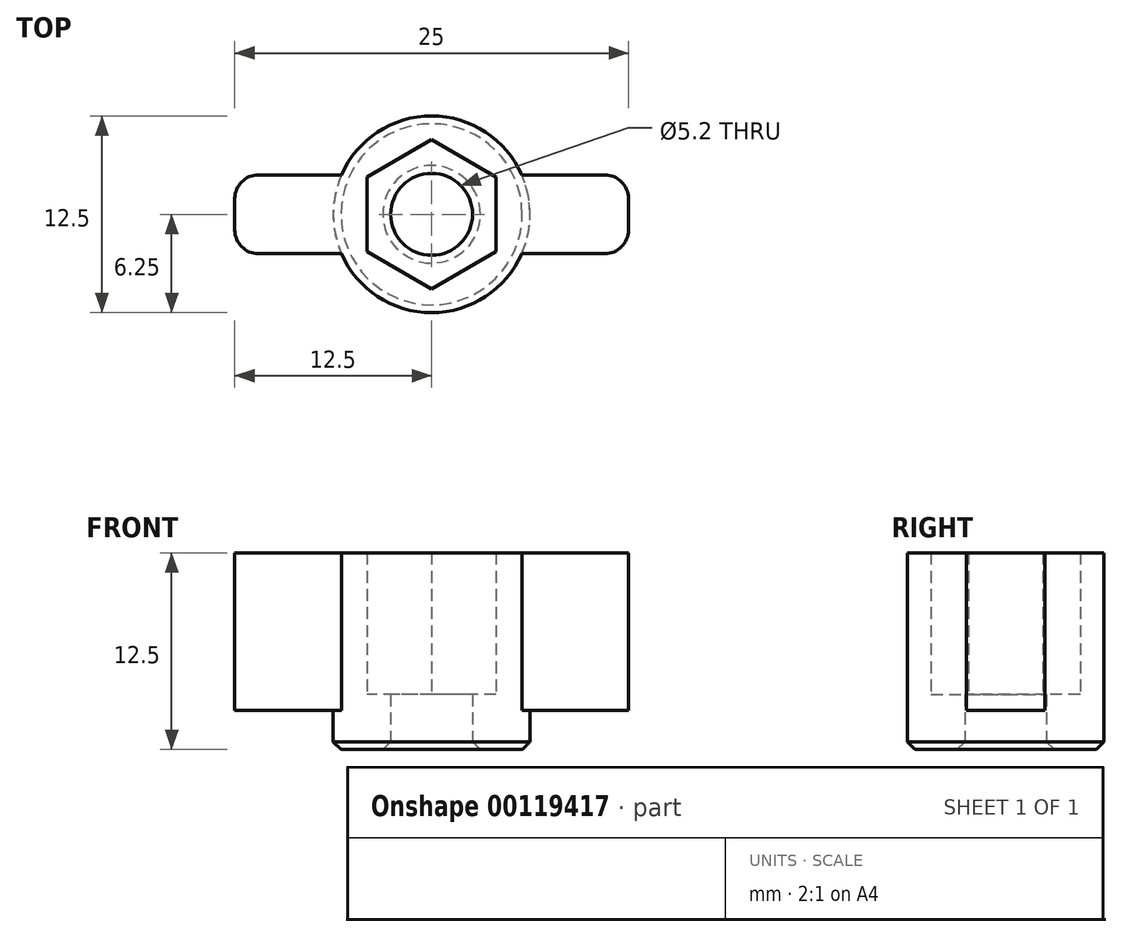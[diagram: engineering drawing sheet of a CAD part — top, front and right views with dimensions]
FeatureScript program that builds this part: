
annotation { "Feature Type Name" : "Feature", "Feature Type Description" : "" }
export const myFeature = defineFeature(function(context is Context, id is Id, definition is map)
    precondition{}
    {
        {
            var Q0;
            Q0=qCreatedBy(makeId("Top.planeOp"),FACE);
            var sketch = newSketch(context, id + "F0", { "sketchPlane" : qUnion([Q0])});
            skCircle(sketch, "E0", {"center": v(0, 0) * mm, "radius": 2.6 * mm});
            skCircle(sketch, "E1", {"center": v(0, 0) * mm, "radius": 6.25 * mm});
            skSolve(sketch);
        }
        {
            var Q0;
            Q0=makeQuery(id+"F0.imprint","IMPRINT",FACE,{"disambiguationData":[TD([[makeQuery(id+"F0.imprint","IMPRINT",EDGE,{"derivedFrom":sQuery(id+"F0.wireOp",EDGE,"E0")}),-1.0]])]});
            extrude(context, id + "F1", {"entities" : qUnion([Q0]), "depth" : 7.5 * mm});
        }
        {
            var Q0;
            Q0=makeQuery(id+"F1.opExtrude","CAP_FACE",FACE,{"disambiguationData":[OSD([sQuery(id+"F0.wireOp",EDGE,"E0"),sQuery(id+"F0.wireOp",EDGE,"E1")])],"isStart":false});
            var sketch = newSketch(context, id + "F2", { "sketchPlane" : qUnion([Q0])});
            skArc(sketch, "E2", {"start": v(5.73, 2.5) * mm, "mid": v(0, 6.25) * mm, "end": v(-5.73, 2.5) * mm});
            skLineSegment(sketch, "E3.bottom", {"start": v(11, -2.5) * mm, "end": v(5.73, -2.5) * mm});
            skLineSegment(sketch, "E3.top", {"start": v(11, 2.5) * mm, "end": v(5.73, 2.5) * mm});
            skLineSegment(sketch, "E3.left", {"start": v(12.5, -1) * mm, "end": v(12.5, 1) * mm});
            skLineSegment(sketch, "E3.right", {"start": v(-12.5, -1) * mm, "end": v(-12.5, 1) * mm});
            skLineSegment(sketch, "E4.trimOffspring", {"start": v(-5.73, 2.5) * mm, "end": v(-11, 2.5) * mm});
            skLineSegment(sketch, "E5.trimOffspring", {"start": v(-5.73, -2.5) * mm, "end": v(-11, -2.5) * mm});
            skArc(sketch, "E6.trimOffspring", {"start": v(-5.73, -2.5) * mm, "mid": v(0, -6.25) * mm, "end": v(5.73, -2.5) * mm});
            skPoint(sketch, "E7.visualSharp", {"position": v(-12.5, 2.5) * mm});
            skArc(sketch, "E7.filletArc", {"start": v(-11, 2.5) * mm, "mid": v(-12.06, 2.06) * mm, "end": v(-12.5, 1) * mm});
            skPoint(sketch, "E8.visualSharp", {"position": v(12.5, 2.5) * mm});
            skArc(sketch, "E8.filletArc", {"start": v(12.5, 1) * mm, "mid": v(12.06, 2.06) * mm, "end": v(11, 2.5) * mm});
            skPoint(sketch, "E9.visualSharp", {"position": v(12.5, -2.5) * mm});
            skArc(sketch, "E9.filletArc", {"start": v(11, -2.5) * mm, "mid": v(12.06, -2.06) * mm, "end": v(12.5, -1) * mm});
            skPoint(sketch, "E10.visualSharp", {"position": v(-12.5, -2.5) * mm});
            skArc(sketch, "E10.filletArc", {"start": v(-12.5, -1) * mm, "mid": v(-12.06, -2.06) * mm, "end": v(-11, -2.5) * mm});
            skCircle(sketch, "E11.cCircle", {"center": v(0, 0) * mm, "radius": 4.1 * mm, "construction": true});
            skLineSegment(sketch, "E11.0", {"start": v(0, 4.73) * mm, "end": v(4.1, 2.37) * mm});
            skLineSegment(sketch, "E11.1", {"start": v(4.1, 2.37) * mm, "end": v(4.1, -2.37) * mm});
            skLineSegment(sketch, "E11.2", {"start": v(4.1, -2.37) * mm, "end": v(0, -4.73) * mm});
            skLineSegment(sketch, "E11.3", {"start": v(0, -4.73) * mm, "end": v(-4.1, -2.37) * mm});
            skLineSegment(sketch, "E11.4", {"start": v(-4.1, -2.37) * mm, "end": v(-4.1, 2.37) * mm});
            skLineSegment(sketch, "E11.5", {"start": v(-4.1, 2.37) * mm, "end": v(0, 4.73) * mm});
            skPoint(sketch, "E11.0.midPoint", {"position": v(2.05, 3.55) * mm});
            skSolve(sketch);
        }
        {
            var Q0;
            Q0=makeQuery(id+"F2.imprint","IMPRINT",FACE,{"disambiguationData":[TD([[makeQuery(id+"F2.imprint","IMPRINT",EDGE,{"derivedFrom":sQuery(id+"F2.wireOp",EDGE,"OllCn0WL-B3th-Vf9Y-IIcn-ZCFhtX2VXAmh")}),-1.0]])]});
            var Q1;
            {var subQ1=sQuery(id+"F2.wireOp",EDGE,"E3.bottom");Q1=makeQuery(id+"F2.imprint","IMPRINT",FACE,{"disambiguationData":[TD([[makeQuery(id+"F2.imprint","IMPRINT",EDGE,{"derivedFrom":subQ1}),-1.0]])]});}
            var Q2;
            Q2=makeQuery(id+"F2.imprint","IMPRINT",FACE,{"disambiguationData":[TD([[makeQuery(id+"F2.imprint","IMPRINT",EDGE,{"derivedFrom":sQuery(id+"F2.wireOp",EDGE,"E3.right")}),-1.0]])]});
            var Q3;
            {var subQ1=sQuery(id+"F2.wireOp",EDGE,"E2");Q3=makeQuery(id+"F2.imprint","IMPRINT",FACE,{"disambiguationData":[TD([[makeQuery(id+"F2.imprint","IMPRINT",EDGE,{"derivedFrom":subQ1}),1.0]])]});}
            extrude(context, id + "F3", {"entities" : qUnion([Q0, Q1, Q2, Q3]), "operationType" : NewBodyOperationType.ADD, "endBound" : BoundingType.SYMMETRIC, "depth" : 10 * mm});
        }
        {
            var Q0;
            Q0=makeQuery(id+"F1.opExtrude","CAP_EDGE",EDGE,{"disambiguationData":[OSD([sQuery(id+"F0.wireOp",EDGE,"E1")])],"isStart":true});
            var Q1;
            Q1=makeQuery(id+"F1.opExtrude","CAP_EDGE",EDGE,{"disambiguationData":[OSD([sQuery(id+"F0.wireOp",EDGE,"E0")])],"isStart":true});
            chamfer(context, id + "F4", {"entities" : qUnion([Q0, Q1]), "width" : .5 * mm, "tangentPropagation" : true});
        }
        {
            var Q0;
            Q0=makeQuery(id+"F1.opExtrude","CAP_FACE",FACE,{"disambiguationData":[OSD([sQuery(id+"F0.wireOp",EDGE,"E0"),sQuery(id+"F0.wireOp",EDGE,"E1")])],"isStart":false});
            var sketch = newSketch(context, id + "F5", { "sketchPlane" : qUnion([Q0])});
            skLineSegment(sketch, "E12", {"start": v(4.1, 2.37) * mm, "end": v(0, 4.73) * mm});
            skLineSegment(sketch, "E13", {"start": v(4.1, -2.37) * mm, "end": v(4.1, 2.37) * mm});
            skLineSegment(sketch, "E14", {"start": v(0, -4.73) * mm, "end": v(4.1, -2.37) * mm});
            skLineSegment(sketch, "E15", {"start": v(-4.1, -2.37) * mm, "end": v(0, -4.73) * mm});
            skLineSegment(sketch, "E16", {"start": v(-4.1, 2.37) * mm, "end": v(-4.1, -2.37) * mm});
            skLineSegment(sketch, "E17", {"start": v(0, 4.73) * mm, "end": v(-4.1, 2.37) * mm});
            skCircle(sketch, "E18", {"center": v(0, 0) * mm, "radius": 2.6 * mm});
            skSolve(sketch);
        }
        {
            var Q0;
            Q0=makeQuery(id+"F5.imprint","IMPRINT",FACE,{"disambiguationData":[TD([[makeQuery(id+"F5.imprint","IMPRINT",EDGE,{"derivedFrom":sQuery(id+"F5.wireOp",EDGE,"E12")}),1.0]])]});
            extrude(context, id + "F6", {"entities" : qUnion([Q0]), "operationType" : NewBodyOperationType.REMOVE, "oppositeDirection" : true, "depth" : 4 * mm});
        }
    });
